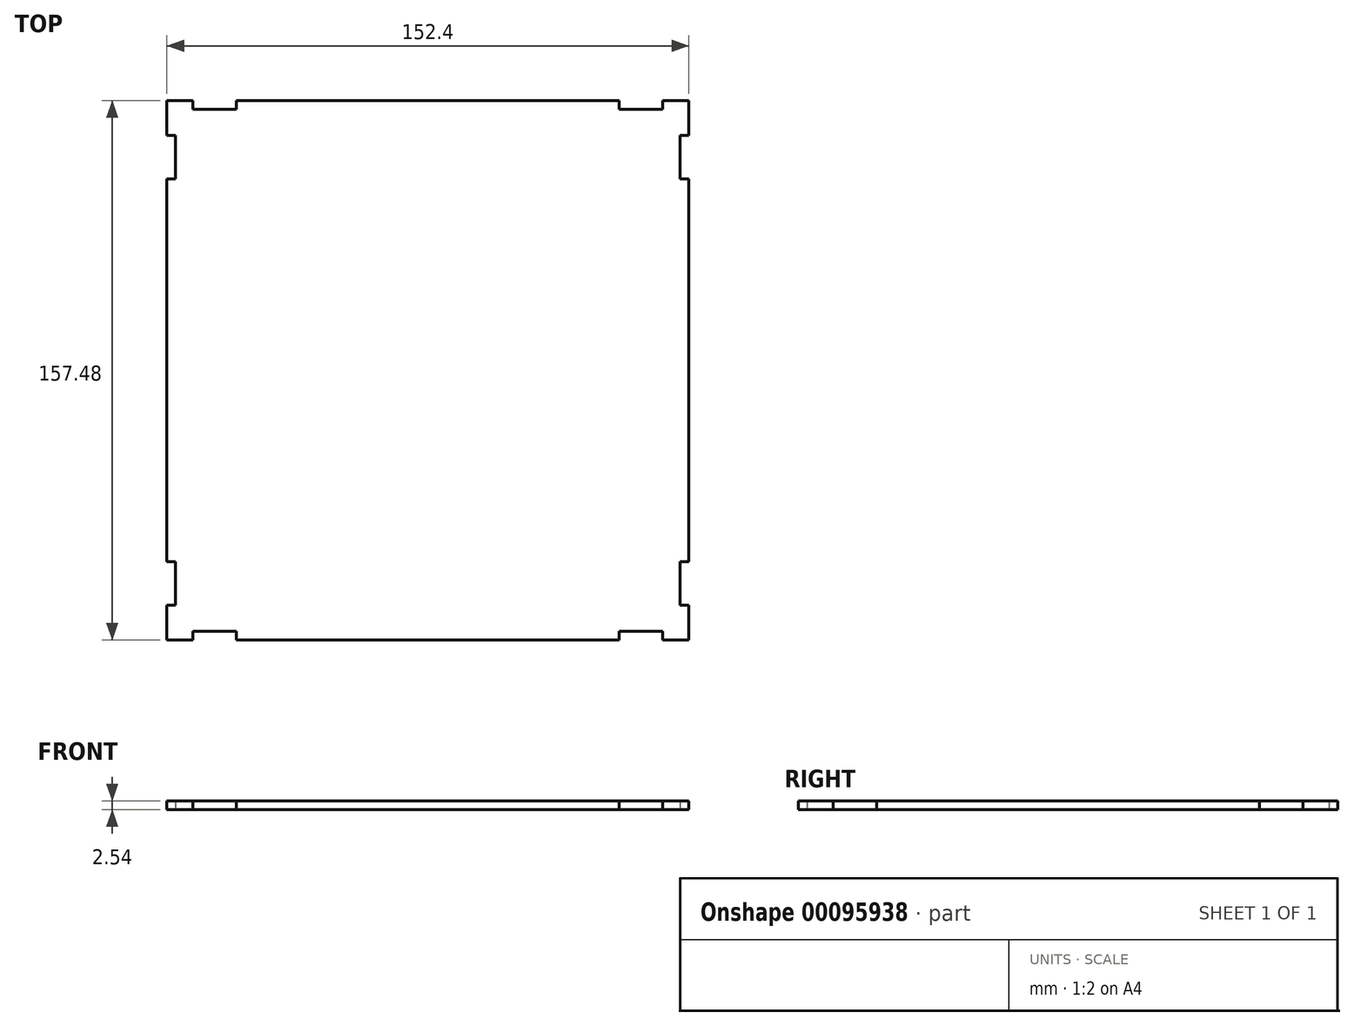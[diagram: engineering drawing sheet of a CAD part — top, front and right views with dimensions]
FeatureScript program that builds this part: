
annotation { "Feature Type Name" : "Feature", "Feature Type Description" : "" }
export const myFeature = defineFeature(function(context is Context, id is Id, definition is map)
    precondition{}
    {
        {
            var Q0;
            Q0=qCreatedBy(makeId("Top.planeOp"),FACE);
            var sketch = newSketch(context, id + "F0", { "sketchPlane" : qUnion([Q0])});
            skLineSegment(sketch, "E0.left", {"start": v(76.2, 76.2) * mm, "end": v(76.2, -76.2) * mm});
            skLineSegment(sketch, "E0.right", {"start": v(-76.2, 76.2) * mm, "end": v(-76.2, -76.2) * mm});
            skPoint(sketch, "E0.middle", {"position": v(0, 0) * mm});
            skLineSegment(sketch, "E1.bottom", {"start": v(-68.58, 76.2) * mm, "end": v(-55.88, 76.2) * mm});
            skLineSegment(sketch, "E2.bottom", {"start": v(76.2, 68.58) * mm, "end": v(73.66, 68.58) * mm});
            skLineSegment(sketch, "E2.left", {"start": v(76.2, 68.58) * mm, "end": v(76.2, 55.88) * mm});
            skLineSegment(sketch, "E3.MirrorCS", {"start": v(76.2, -55.88) * mm, "end": v(73.66, -55.88) * mm});
            skLineSegment(sketch, "E4.MirrorCS", {"start": v(73.66, -68.58) * mm, "end": v(73.66, -55.88) * mm});
            skLineSegment(sketch, "E5.MirrorCS", {"start": v(76.2, -68.58) * mm, "end": v(73.66, -68.58) * mm});
            skLineSegment(sketch, "E6.MirrorCS", {"start": v(-73.66, 68.58) * mm, "end": v(-73.66, 55.88) * mm});
            skLineSegment(sketch, "E7.MirrorCS", {"start": v(-76.2, 55.88) * mm, "end": v(-73.66, 55.88) * mm});
            skLineSegment(sketch, "E8.MirrorCS", {"start": v(-76.2, 68.58) * mm, "end": v(-73.66, 68.58) * mm});
            skLineSegment(sketch, "E9.MirrorCS", {"start": v(-76.2, -55.88) * mm, "end": v(-73.66, -55.88) * mm});
            skLineSegment(sketch, "E10.MirrorCS", {"start": v(-73.66, -68.58) * mm, "end": v(-73.66, -55.88) * mm});
            skLineSegment(sketch, "E11.MirrorCS", {"start": v(-76.2, -68.58) * mm, "end": v(-73.66, -68.58) * mm});
            skLineSegment(sketch, "E12", {"start": v(76.2, 55.88) * mm, "end": v(73.66, 55.88) * mm});
            skLineSegment(sketch, "E13", {"start": v(73.66, 68.58) * mm, "end": v(73.66, 55.88) * mm});
            skLineSegment(sketch, "E14.top", {"start": v(-76.2, -78.74) * mm, "end": v(76.2, -78.74) * mm});
            skLineSegment(sketch, "E14.left", {"start": v(-76.2, -76.2) * mm, "end": v(-76.2, -78.74) * mm});
            skLineSegment(sketch, "E14.right", {"start": v(76.2, -76.2) * mm, "end": v(76.2, -78.74) * mm});
            skLineSegment(sketch, "E15.bottom", {"start": v(-68.58, -76.2) * mm, "end": v(-55.88, -76.2) * mm});
            skLineSegment(sketch, "E15.top", {"start": v(-68.58, -78.74) * mm, "end": v(-55.88, -78.74) * mm});
            skLineSegment(sketch, "E15.left", {"start": v(-68.58, -76.2) * mm, "end": v(-68.58, -78.74) * mm});
            skLineSegment(sketch, "E15.right", {"start": v(-55.88, -76.2) * mm, "end": v(-55.88, -78.74) * mm});
            skLineSegment(sketch, "E16.bottom", {"start": v(55.88, -76.2) * mm, "end": v(68.58, -76.2) * mm});
            skLineSegment(sketch, "E16.top", {"start": v(55.88, -78.74) * mm, "end": v(68.58, -78.74) * mm});
            skLineSegment(sketch, "E16.left", {"start": v(55.88, -76.2) * mm, "end": v(55.88, -78.74) * mm});
            skLineSegment(sketch, "E16.right", {"start": v(68.58, -76.2) * mm, "end": v(68.58, -78.74) * mm});
            skLineSegment(sketch, "E17.top", {"start": v(-76.2, 78.74) * mm, "end": v(76.2, 78.74) * mm});
            skLineSegment(sketch, "E17.left", {"start": v(-76.2, 76.2) * mm, "end": v(-76.2, 78.74) * mm});
            skLineSegment(sketch, "E17.right", {"start": v(76.2, 76.2) * mm, "end": v(76.2, 78.74) * mm});
            skLineSegment(sketch, "E18.top", {"start": v(-68.58, 78.74) * mm, "end": v(-55.88, 78.74) * mm});
            skLineSegment(sketch, "E18.left", {"start": v(-68.58, 76.2) * mm, "end": v(-68.58, 78.74) * mm});
            skLineSegment(sketch, "E18.right", {"start": v(-55.88, 76.2) * mm, "end": v(-55.88, 78.74) * mm});
            skLineSegment(sketch, "E19.bottom", {"start": v(55.88, 76.2) * mm, "end": v(68.58, 76.2) * mm});
            skLineSegment(sketch, "E19.top", {"start": v(55.88, 78.74) * mm, "end": v(68.58, 78.74) * mm});
            skLineSegment(sketch, "E19.left", {"start": v(55.88, 76.2) * mm, "end": v(55.88, 78.74) * mm});
            skLineSegment(sketch, "E19.right", {"start": v(68.58, 76.2) * mm, "end": v(68.58, 78.74) * mm});
            skSolve(sketch);
        }
        {
            var Q0;
            {var subQ10=sQuery(id+"F0.wireOp",EDGE,"E2.bottom");Q0=makeQuery(id+"F0.imprint","IMPRINT",FACE,{"disambiguationData":[TD([[makeQuery(id+"F0.imprint","IMPRINT",EDGE,{"derivedFrom":subQ10}),-1.0]])]});}
            extrude(context, id + "F1", {"entities" : qUnion([Q0]), "depth" : 2.54 * mm});
        }
    });
